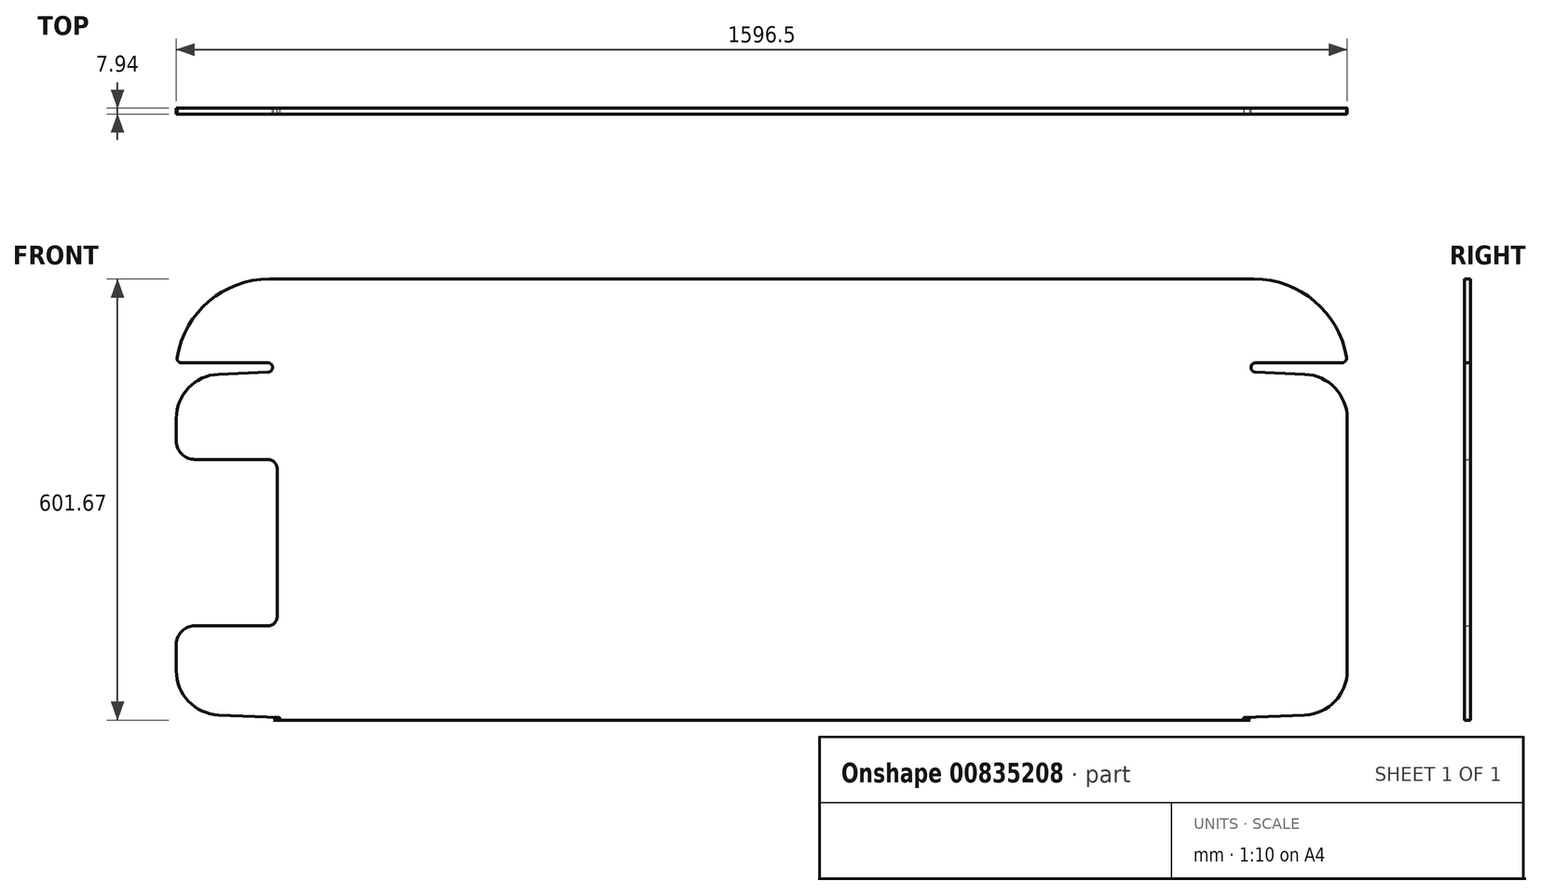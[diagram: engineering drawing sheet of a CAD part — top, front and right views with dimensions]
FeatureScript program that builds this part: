
annotation { "Feature Type Name" : "Feature", "Feature Type Description" : "" }
export const myFeature = defineFeature(function(context is Context, id is Id, definition is map)
    precondition{}
    {
        {
            var Q0;
            Q0=qCreatedBy(makeId("Front.planeOp"),FACE);
            var sketch = newSketch(context, id + "F0", { "sketchPlane" : qUnion([Q0])});
            skLineSegment(sketch, "E0", {"start": v(-665.95, -251.37) * mm, "end": v(-653.68, -248.08) * mm});
            skLineSegment(sketch, "E1", {"start": v(-653.68, -248.08) * mm, "end": v(-740.56, -244.29) * mm});
            skArc(sketch, "E2", {"start": v(-740.56, -244.29) * mm, "mid": v(-781.5, -225.73) * mm, "end": v(-798.25, -184.02) * mm});
            skLineSegment(sketch, "E3", {"start": v(-798.25, -184.02) * mm, "end": v(-798.25, -148.18) * mm});
            skLineSegment(sketch, "E4", {"start": v(-772.85, -122.78) * mm, "end": v(-673.35, -122.78) * mm});
            skLineSegment(sketch, "E5", {"start": v(-660.65, -110.08) * mm, "end": v(-660.65, 91.53) * mm});
            skLineSegment(sketch, "E6", {"start": v(-673.35, 104.23) * mm, "end": v(-772.85, 104.23) * mm});
            skLineSegment(sketch, "E7", {"start": v(-798.25, 129.63) * mm, "end": v(-798.25, 160.09) * mm});
            skArc(sketch, "E8", {"start": v(-798.25, 160.09) * mm, "mid": v(-781.5, 201.8) * mm, "end": v(-740.56, 220.36) * mm});
            skLineSegment(sketch, "E9", {"start": v(-740.56, 220.36) * mm, "end": v(-673.07, 223.3) * mm});
            skPoint(sketch, "E10.visualSharp", {"position": v(-671.25, -122.78) * mm});
            skArc(sketch, "E10.filletArc", {"start": v(-673.35, -122.78) * mm, "mid": v(-664.37, -119.06) * mm, "end": v(-660.65, -110.08) * mm});
            skPoint(sketch, "E11.visualSharp", {"position": v(-660.65, 104.23) * mm});
            skArc(sketch, "E11.filletArc", {"start": v(-660.65, 91.53) * mm, "mid": v(-664.37, 100.51) * mm, "end": v(-673.35, 104.23) * mm});
            skPoint(sketch, "E12.visualSharp", {"position": v(-798.25, 104.23) * mm});
            skArc(sketch, "E12.filletArc", {"start": v(-798.25, 129.63) * mm, "mid": v(-790.81, 111.67) * mm, "end": v(-772.85, 104.23) * mm});
            skPoint(sketch, "E13.visualSharp", {"position": v(-798.25, -122.78) * mm});
            skArc(sketch, "E13.filletArc", {"start": v(-772.85, -122.78) * mm, "mid": v(-790.81, -130.22) * mm, "end": v(-798.25, -148.18) * mm});
            skArc(sketch, "E14", {"start": v(-673.07, 223.3) * mm, "mid": v(-667, 229.79) * mm, "end": v(-673.35, 236) * mm});
            skLineSegment(sketch, "E15", {"start": v(-673.35, 236) * mm, "end": v(-790.99, 236) * mm});
            skArc(sketch, "E16", {"start": v(-671.25, 350.3) * mm, "mid": v(-753.88, 319.97) * mm, "end": v(-797.25, 243.38) * mm});
            skLineSegment(sketch, "E17", {"start": v(-671.25, 350.3) * mm, "end": v(671.25, 350.3) * mm});
            skPoint(sketch, "E18.visualSharp", {"position": v(-798.25, 236) * mm});
            skArc(sketch, "E18.filletArc", {"start": v(-797.25, 243.38) * mm, "mid": v(-795.83, 238.24) * mm, "end": v(-790.99, 236) * mm});
            skLineSegment(sketch, "E19", {"start": v(0, -314.87) * mm, "end": v(0, 428.95) * mm, "construction": true});
            skArc(sketch, "E20.MirrorCS", {"start": v(671.25, 350.3) * mm, "mid": v(753.88, 319.97) * mm, "end": v(797.25, 243.38) * mm});
            skArc(sketch, "E21.MirrorCS", {"start": v(797.25, 243.38) * mm, "mid": v(795.83, 238.24) * mm, "end": v(790.99, 236) * mm});
            skLineSegment(sketch, "E22.MirrorCS", {"start": v(673.35, 236) * mm, "end": v(790.99, 236) * mm});
            skArc(sketch, "E23.MirrorCS", {"start": v(673.07, 223.3) * mm, "mid": v(667, 229.79) * mm, "end": v(673.35, 236) * mm});
            skLineSegment(sketch, "E24.MirrorCS", {"start": v(740.56, 220.36) * mm, "end": v(673.07, 223.3) * mm});
            skArc(sketch, "E25.MirrorCS", {"start": v(798.25, 160.09) * mm, "mid": v(781.5, 201.8) * mm, "end": v(740.56, 220.36) * mm});
            skLineSegment(sketch, "E26.MirrorCS", {"start": v(665.95, -251.37) * mm, "end": v(653.68, -248.08) * mm});
            skLineSegment(sketch, "E27.MirrorCS", {"start": v(653.68, -248.08) * mm, "end": v(740.56, -244.29) * mm});
            skArc(sketch, "E28.MirrorCS", {"start": v(740.56, -244.29) * mm, "mid": v(781.5, -225.73) * mm, "end": v(798.25, -184.02) * mm});
            skLineSegment(sketch, "E29", {"start": v(798.25, 160.09) * mm, "end": v(798.25, -184.02) * mm});
            skLineSegment(sketch, "E30", {"start": v(665.95, -251.37) * mm, "end": v(-665.95, -251.37) * mm});
            skSolve(sketch);
        }
        {
            var Q0;
            Q0 = qSketchRegion(id + "F0", true);
            extrude(context, id + "F1", {"entities" : qUnion([Q0]), "depth" : 7.94 * mm, "offsetDistance" : 25.4 * mm});
        }
        {
            var Q0;
            Q0=makeQuery(id+"F1.opExtrude","SWEPT_EDGE",EDGE,{"disambiguationData":[OSD([sQuery(id+"F0.wireOp",EDGE,"E0"),sQuery(id+"F0.wireOp",EDGE,"E1")])]});
            var Q1;
            Q1=makeQuery(id+"F1.opExtrude","SWEPT_EDGE",EDGE,{"disambiguationData":[OSD([sQuery(id+"F0.wireOp",EDGE,"E26.MirrorCS"),sQuery(id+"F0.wireOp",EDGE,"E27.MirrorCS")])]});
            fillet(context, id + "F2", {"entities" : qUnion([Q0, Q1]), "radius" : 0.64 * mm, "tangentPropagation" : true, "allowEdgeOverflow" : false});
        }
    });
